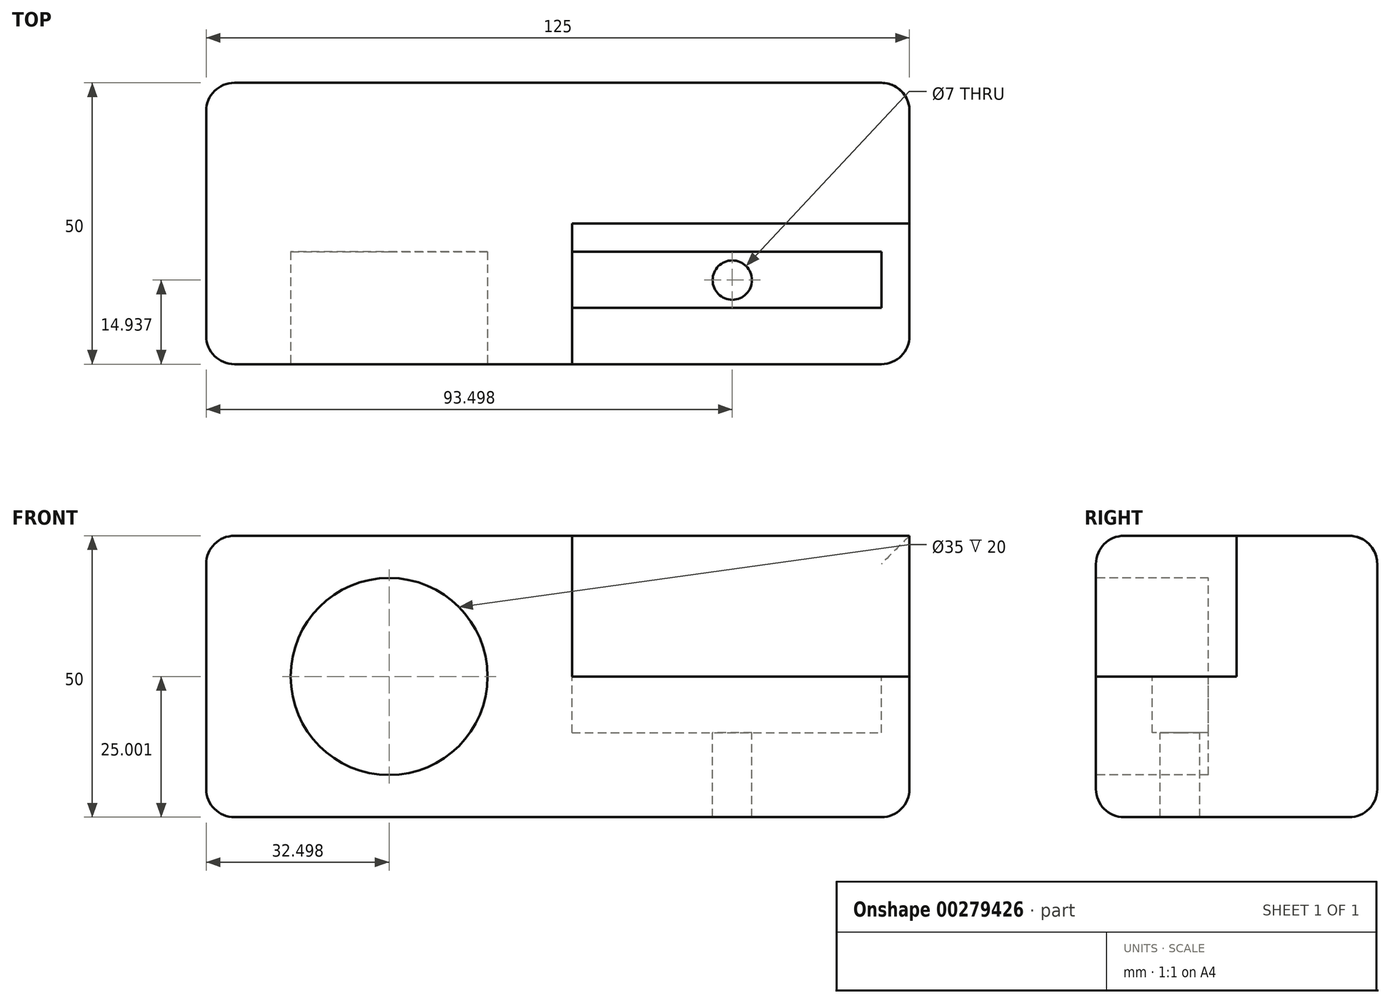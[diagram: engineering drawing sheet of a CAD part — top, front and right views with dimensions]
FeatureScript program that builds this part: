
annotation { "Feature Type Name" : "Feature", "Feature Type Description" : "" }
export const myFeature = defineFeature(function(context is Context, id is Id, definition is map)
    precondition{}
    {
        {
            var Q0;
            Q0=qCreatedBy(makeId("Front.planeOp"),FACE);
            var sketch = newSketch(context, id + "F0", { "sketchPlane" : qUnion([Q0])});
            skLineSegment(sketch, "E0.bottom", {"start": v(-58.26, 27.77) * mm, "end": v(66.74, 27.77) * mm});
            skLineSegment(sketch, "E0.top", {"start": v(-58.26, -22.23) * mm, "end": v(66.74, -22.23) * mm});
            skLineSegment(sketch, "E0.left", {"start": v(-58.26, 27.77) * mm, "end": v(-58.26, -22.23) * mm});
            skLineSegment(sketch, "E0.right", {"start": v(66.74, 27.77) * mm, "end": v(66.74, -22.23) * mm});
            skSolve(sketch);
        }
        {
            var Q0;
            Q0=makeQuery(id+"F0.imprint","IMPRINT",FACE,{"disambiguationData":[TD([[makeQuery(id+"F0.imprint","IMPRINT",EDGE,{"derivedFrom":sQuery(id+"F0.wireOp",EDGE,"E0.bottom")}),-1.0]])]});
            extrude(context, id + "F1", {"entities" : qUnion([Q0]), "depth" : 50 * mm});
        }
        {
            var Q0;
            Q0=makeQuery(id+"F1.opExtrude","CAP_FACE",FACE,{"disambiguationData":[OSD([sQuery(id+"F0.wireOp",EDGE,"E0.bottom"),sQuery(id+"F0.wireOp",EDGE,"E0.top"),sQuery(id+"F0.wireOp",EDGE,"E0.left"),sQuery(id+"F0.wireOp",EDGE,"E0.right")])],"isStart":false});
            var sketch = newSketch(context, id + "F2", { "sketchPlane" : qUnion([Q0])});
            skLineSegment(sketch, "E1.bottom", {"start": v(6.74, 27.77) * mm, "end": v(66.74, 27.77) * mm});
            skLineSegment(sketch, "E1.top", {"start": v(6.74, 2.77) * mm, "end": v(66.74, 2.77) * mm});
            skLineSegment(sketch, "E1.left", {"start": v(6.74, 27.77) * mm, "end": v(6.74, 2.77) * mm});
            skLineSegment(sketch, "E1.right", {"start": v(66.74, 27.77) * mm, "end": v(66.74, 2.77) * mm});
            skSolve(sketch);
        }
        {
            var Q0;
            Q0 = qSketchRegion(id + "F2", true);
            extrude(context, id + "F3", {"entities" : qUnion([Q0]), "operationType" : NewBodyOperationType.REMOVE, "oppositeDirection" : true, "depth" : 25 * mm});
        }
        {
            var Q0;
            Q0=makeQuery(id+"F1.opExtrude","CAP_FACE",FACE,{"disambiguationData":[OSD([sQuery(id+"F0.wireOp",EDGE,"E0.bottom"),sQuery(id+"F0.wireOp",EDGE,"E0.top"),sQuery(id+"F0.wireOp",EDGE,"E0.left"),sQuery(id+"F0.wireOp",EDGE,"E0.right")])],"isStart":false});
            var sketch = newSketch(context, id + "F4", { "sketchPlane" : qUnion([Q0])});
            skCircle(sketch, "E2", {"center": v(-25.76, 2.77) * mm, "radius": 17.5 * mm});
            skSolve(sketch);
        }
        {
            var Q0;
            Q0 = qSketchRegion(id + "F4", true);
            extrude(context, id + "F5", {"entities" : qUnion([Q0]), "operationType" : NewBodyOperationType.REMOVE, "oppositeDirection" : true, "depth" : 20 * mm});
        }
        {
            var Q0;
            Q0=makeQuery(id+"F1.opExtrude","CAP_EDGE",EDGE,{"disambiguationData":[OSD([sQuery(id+"F0.wireOp",EDGE,"E0.bottom")])],"isStart":false});
            var Q1;
            Q1=makeQuery(id+"F1.opExtrude","CAP_EDGE",EDGE,{"disambiguationData":[OSD([sQuery(id+"F0.wireOp",EDGE,"E0.left")])],"isStart":false});
            var Q2;
            Q2=makeQuery(id+"F1.opExtrude","CAP_EDGE",EDGE,{"disambiguationData":[OSD([sQuery(id+"F0.wireOp",EDGE,"E0.top")])],"isStart":false});
            var Q3;
            Q3=makeQuery(id+"F1.opExtrude","CAP_EDGE",EDGE,{"disambiguationData":[OSD([sQuery(id+"F0.wireOp",EDGE,"E0.right")])],"isStart":false});
            var Q4;
            Q4=makeQuery(id+"F3.boolean.opBoolean","COPY",EDGE,{"derivedFrom":makeQuery(id+"F3.opExtrude","CAP_EDGE",EDGE,{"disambiguationData":[OSD([sQuery(id+"F2.wireOp",EDGE,"E1.top")])],"isStart":true})});
            var Q5;
            Q5=makeQuery(id+"F3.boolean.opBoolean","COPY",EDGE,{"derivedFrom":makeQuery(id+"F3.opExtrude","CAP_EDGE",EDGE,{"disambiguationData":[OSD([sQuery(id+"F2.wireOp",EDGE,"E1.left")])],"isStart":true})});
            var Q6;
            Q6=makeQuery(id+"F3.boolean.opBoolean","COPY",EDGE,{"derivedFrom":makeQuery(id+"F3.opExtrude","SWEPT_EDGE",EDGE,{"disambiguationData":[OSD([sQuery(id+"F0.wireOp",EDGE,"E0.bottom"),sQuery(id+"F2.wireOp",EDGE,"E1.bottom"),sQuery(id+"F2.wireOp",EDGE,"E1.left")])]})});
            var Q7;
            Q7=makeQuery(id+"F3.boolean.opBoolean","COPY",EDGE,{"derivedFrom":makeQuery(id+"F3.opExtrude","CAP_EDGE",EDGE,{"disambiguationData":[OSD([sQuery(id+"F2.wireOp",EDGE,"E1.bottom")])],"isStart":false})});
            var Q8;
            Q8=makeQuery(id+"F3.boolean.opBoolean","COPY",EDGE,{"derivedFrom":makeQuery(id+"F3.opExtrude","CAP_EDGE",EDGE,{"disambiguationData":[OSD([sQuery(id+"F2.wireOp",EDGE,"E1.right")])],"isStart":false})});
            var Q9;
            Q9=makeQuery(id+"F3.boolean.opBoolean","COPY",EDGE,{"derivedFrom":makeQuery(id+"F3.opExtrude","SWEPT_EDGE",EDGE,{"disambiguationData":[OSD([sQuery(id+"F0.wireOp",EDGE,"E0.right"),sQuery(id+"F2.wireOp",EDGE,"E1.top"),sQuery(id+"F2.wireOp",EDGE,"E1.right")])]})});
            var Q10;
            Q10=makeQuery(id+"F1.opExtrude","SWEPT_EDGE",EDGE,{"disambiguationData":[OSD([sQuery(id+"F0.wireOp",EDGE,"E0.top"),sQuery(id+"F0.wireOp",EDGE,"E0.right")])]});
            var Q11;
            Q11=makeQuery(id+"F1.opExtrude","CAP_EDGE",EDGE,{"disambiguationData":[OSD([sQuery(id+"F0.wireOp",EDGE,"E0.right")])],"isStart":true});
            var Q12;
            Q12=makeQuery(id+"F1.opExtrude","CAP_EDGE",EDGE,{"disambiguationData":[OSD([sQuery(id+"F0.wireOp",EDGE,"E0.bottom")])],"isStart":true});
            var Q13;
            Q13=makeQuery(id+"F1.opExtrude","CAP_EDGE",EDGE,{"disambiguationData":[OSD([sQuery(id+"F0.wireOp",EDGE,"E0.top")])],"isStart":true});
            var Q14;
            Q14=makeQuery(id+"F1.opExtrude","CAP_EDGE",EDGE,{"disambiguationData":[OSD([sQuery(id+"F0.wireOp",EDGE,"E0.left")])],"isStart":true});
            var Q15;
            Q15=makeQuery(id+"F1.opExtrude","SWEPT_EDGE",EDGE,{"disambiguationData":[OSD([sQuery(id+"F0.wireOp",EDGE,"E0.bottom"),sQuery(id+"F0.wireOp",EDGE,"E0.left")])]});
            var Q16;
            Q16=makeQuery(id+"F1.opExtrude","SWEPT_EDGE",EDGE,{"disambiguationData":[OSD([sQuery(id+"F0.wireOp",EDGE,"E0.top"),sQuery(id+"F0.wireOp",EDGE,"E0.left")])]});
            fillet(context, id + "F6", {"entities" : qUnion([Q0, Q1, Q2, Q3, Q4, Q5, Q6, Q7, Q8, Q9, Q10, Q11, Q12, Q13, Q14, Q15, Q16]), "radius" : 5 * mm, "tangentPropagation" : true, "allowEdgeOverflow" : false});
        }
        {
            var Q0;
            Q0=makeQuery(id+"F3.boolean.opBoolean","COPY",FACE,{"derivedFrom":makeQuery(id+"F3.opExtrude","SWEPT_FACE",FACE,{"disambiguationData":[OSD([sQuery(id+"F2.wireOp",EDGE,"E1.top")])]})});
            var sketch = newSketch(context, id + "F7", { "sketchPlane" : qUnion([Q0])});
            skLineSegment(sketch, "E3.bottom", {"start": v(6.74, -40) * mm, "end": v(61.74, -40) * mm});
            skLineSegment(sketch, "E3.top", {"start": v(6.74, -30) * mm, "end": v(61.74, -30) * mm});
            skLineSegment(sketch, "E3.left", {"start": v(6.74, -40) * mm, "end": v(6.74, -30) * mm});
            skLineSegment(sketch, "E3.right", {"start": v(61.74, -40) * mm, "end": v(61.74, -30) * mm});
            skSolve(sketch);
        }
        {
            var Q0;
            Q0 = qSketchRegion(id + "F7", true);
            extrude(context, id + "F8", {"entities" : qUnion([Q0]), "operationType" : NewBodyOperationType.REMOVE, "oppositeDirection" : true, "depth" : 10 * mm});
        }
        {
            var Q0;
            Q0=makeQuery(id+"F8.boolean.opBoolean","COPY",FACE,{"derivedFrom":makeQuery(id+"F8.opExtrude","CAP_FACE",FACE,{"disambiguationData":[OSD([sQuery(id+"F7.wireOp",EDGE,"E3.bottom"),sQuery(id+"F7.wireOp",EDGE,"E3.top"),sQuery(id+"F7.wireOp",EDGE,"E3.left"),sQuery(id+"F7.wireOp",EDGE,"E3.right")])],"isStart":false})});
            var sketch = newSketch(context, id + "F9", { "sketchPlane" : qUnion([Q0])});
            skCircle(sketch, "E4", {"center": v(35.24, -35.06) * mm, "radius": 3.5 * mm});
            skSolve(sketch);
        }
        {
            var Q0;
            Q0=makeQuery(id+"F9.imprint","IMPRINT",FACE,{"disambiguationData":[TD([[makeQuery(id+"F9.imprint","IMPRINT",EDGE,{"derivedFrom":sQuery(id+"F9.wireOp",EDGE,"E4")}),1.0]])]});
            extrude(context, id + "F10", {"entities" : qUnion([Q0]), "operationType" : NewBodyOperationType.REMOVE, "oppositeDirection" : true, "depth" : 25 * mm});
        }
    });
